# Revit family: Ghent - Champion - 2040 + 2282 Series
name_source: partatom
category: Furniture
units: mm (PartAtom-declared; Revit-internal decimal feet)

## family parameters
Always vertical = Yes
Cut with Voids When Loaded = No
OmniClass Number = 23.40.20.00
OmniClass Title = General Furniture and Specialties
Room Calculation Point = No
Shared = No
Work Plane-Based = No

## types (4) — shared parameters
Bottom Rail Depth = 0' - 0 27/32"
Bracket Support Offset = 0' - 1 1/16"
Manufacturer = Ghent
Side Profile Value = 0' - 0 27/32"
Side Support Offset = 0' - 2 3/4"
URL = https://ghent.com

## per-type parameters (varying)
| type | Depth | Door Panel Width | Half Length Shelves | Height | Shelf Depth | Shelf Tiers | Shelf Width | Width |
| Style 2040 - 48”H x 48”W x 16”D | 1' - 4" | 1' - 11 1/2" | Yes | 4' - 0" | 1' - 2" | 2 | 1' - 11 3/8" | 4' - 0" |
| Style 2040 - 48”H x 60”W x 16”D | 1' - 4" | 2' - 5 1/2" | Yes | 4' - 0" | 1' - 2" | 2 | 2' - 5 3/8" | 5' - 0" |
| Style 2040 - 48”H x 72”W x 16”D | 1' - 4" | 2' - 11 1/2" | Yes | 4' - 0" | 1' - 2" | 2 | 2' - 11 3/8" | 6' - 0" |
| Style 2282 - 30”H x 36”W x 14”D | 1' - 2" | 1' - 5 1/2" | No | 2' - 6" | 1' - 0" | 1 | 2' - 8 5/8" | 3' - 0" |

## geometry (parser evidence)
native form markers: Sweep x13
no freeform markers — native parametric forms only
